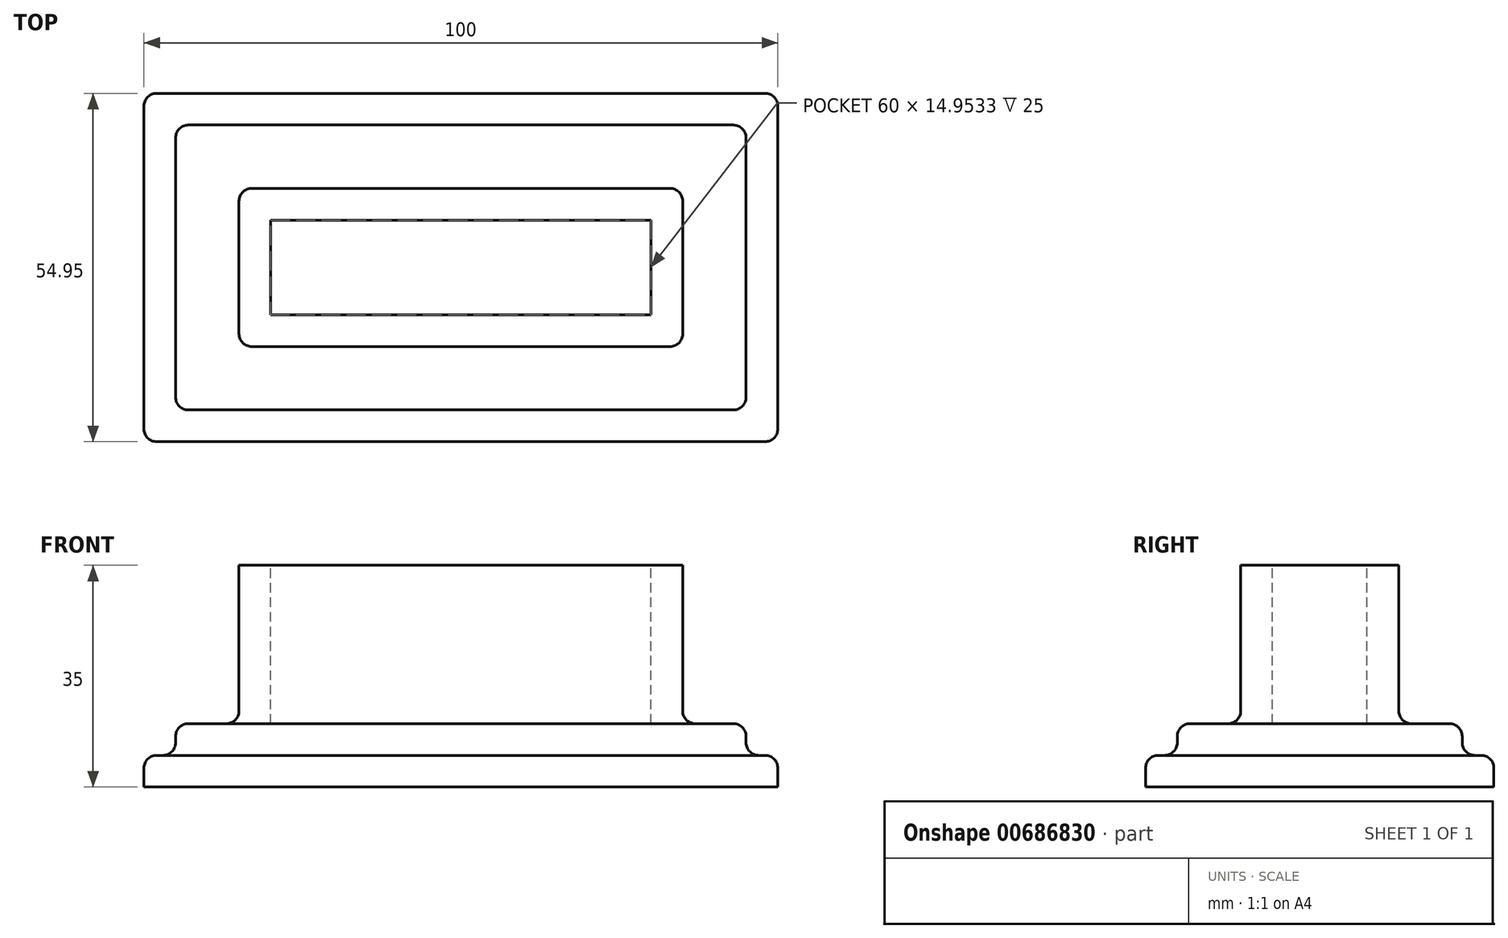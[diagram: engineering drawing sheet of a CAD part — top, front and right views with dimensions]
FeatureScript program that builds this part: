
annotation { "Feature Type Name" : "Feature", "Feature Type Description" : "" }
export const myFeature = defineFeature(function(context is Context, id is Id, definition is map)
    precondition{}
    {
        {
            var Q0;
            Q0=qCreatedBy(makeId("Top.planeOp"),FACE);
            var sketch = newSketch(context, id + "F0", { "sketchPlane" : qUnion([Q0])});
            skLineSegment(sketch, "E0.bottom", {"start": v(-39.07, 25.23) * mm, "end": v(60.93, 25.23) * mm});
            skLineSegment(sketch, "E0.top", {"start": v(-39.07, -29.72) * mm, "end": v(60.93, -29.72) * mm});
            skLineSegment(sketch, "E0.left", {"start": v(-39.07, 25.23) * mm, "end": v(-39.07, -29.72) * mm});
            skLineSegment(sketch, "E0.right", {"start": v(60.93, 25.23) * mm, "end": v(60.93, -29.72) * mm});
            skSolve(sketch);
        }
        {
            var Q0;
            Q0 = qSketchRegion(id + "F0", true);
            extrude(context, id + "F1", {"entities" : qUnion([Q0]), "depth" : 5 * mm, "offsetDistance" : 25 * mm});
        }
        {
            var Q0;
            Q0=makeQuery(id+"F1.opExtrude","CAP_FACE",FACE,{"disambiguationData":[OSD([sQuery(id+"F0.wireOp",EDGE,"E0.bottom"),sQuery(id+"F0.wireOp",EDGE,"E0.top"),sQuery(id+"F0.wireOp",EDGE,"E0.left"),sQuery(id+"F0.wireOp",EDGE,"E0.right")])],"isStart":false});
            var sketch = newSketch(context, id + "F2", { "sketchPlane" : qUnion([Q0])});
            skLineSegment(sketch, "E1.bottom", {"start": v(-34.07, 20.23) * mm, "end": v(55.93, 20.23) * mm});
            skLineSegment(sketch, "E1.top", {"start": v(-34.07, -24.72) * mm, "end": v(55.93, -24.72) * mm});
            skLineSegment(sketch, "E1.left", {"start": v(-34.07, 20.23) * mm, "end": v(-34.07, -24.72) * mm});
            skLineSegment(sketch, "E1.right", {"start": v(55.93, 20.23) * mm, "end": v(55.93, -24.72) * mm});
            skSolve(sketch);
        }
        {
            var Q0;
            Q0 = qSketchRegion(id + "F2", true);
            extrude(context, id + "F3", {"entities" : qUnion([Q0]), "operationType" : NewBodyOperationType.ADD, "depth" : 5 * mm, "offsetDistance" : 25 * mm});
        }
        {
            var Q0;
            Q0=makeQuery(id+"F3.opExtrude","CAP_FACE",FACE,{"disambiguationData":[OSD([sQuery(id+"F2.wireOp",EDGE,"E1.bottom"),sQuery(id+"F2.wireOp",EDGE,"E1.top"),sQuery(id+"F2.wireOp",EDGE,"E1.left"),sQuery(id+"F2.wireOp",EDGE,"E1.right")])],"isStart":false});
            var sketch = newSketch(context, id + "F4", { "sketchPlane" : qUnion([Q0])});
            skLineSegment(sketch, "E2.bottom", {"start": v(-24.07, 10.23) * mm, "end": v(45.93, 10.23) * mm});
            skLineSegment(sketch, "E2.top", {"start": v(-24.07, -14.72) * mm, "end": v(45.93, -14.72) * mm});
            skLineSegment(sketch, "E2.left", {"start": v(-24.07, 10.23) * mm, "end": v(-24.07, -14.72) * mm});
            skLineSegment(sketch, "E2.right", {"start": v(45.93, 10.23) * mm, "end": v(45.93, -14.72) * mm});
            skSolve(sketch);
        }
        {
            var Q0;
            Q0 = qSketchRegion(id + "F4", true);
            extrude(context, id + "F5", {"entities" : qUnion([Q0]), "operationType" : NewBodyOperationType.ADD, "depth" : 25 * mm, "offsetDistance" : 25 * mm});
        }
        {
            var Q0;
            Q0=makeQuery(id+"F1.opExtrude","SWEPT_EDGE",EDGE,{"disambiguationData":[OSD([sQuery(id+"F0.wireOp",EDGE,"E0.bottom"),sQuery(id+"F0.wireOp",EDGE,"E0.right")])]});
            var Q1;
            Q1=makeQuery(id+"F1.opExtrude","SWEPT_EDGE",EDGE,{"disambiguationData":[OSD([sQuery(id+"F0.wireOp",EDGE,"E0.bottom"),sQuery(id+"F0.wireOp",EDGE,"E0.left")])]});
            var Q2;
            Q2=makeQuery(id+"F1.opExtrude","SWEPT_EDGE",EDGE,{"disambiguationData":[OSD([sQuery(id+"F0.wireOp",EDGE,"E0.top"),sQuery(id+"F0.wireOp",EDGE,"E0.left")])]});
            var Q3;
            Q3=makeQuery(id+"F1.opExtrude","SWEPT_EDGE",EDGE,{"disambiguationData":[OSD([sQuery(id+"F0.wireOp",EDGE,"E0.top"),sQuery(id+"F0.wireOp",EDGE,"E0.right")])]});
            var Q4;
            Q4=makeQuery(id+"F5.opExtrude","SWEPT_EDGE",EDGE,{"disambiguationData":[OSD([sQuery(id+"F4.wireOp",EDGE,"E2.top"),sQuery(id+"F4.wireOp",EDGE,"E2.right")])]});
            var Q5;
            Q5=makeQuery(id+"F5.opExtrude","SWEPT_EDGE",EDGE,{"disambiguationData":[OSD([sQuery(id+"F4.wireOp",EDGE,"E2.bottom"),sQuery(id+"F4.wireOp",EDGE,"E2.right")])]});
            var Q6;
            Q6=makeQuery(id+"F3.opExtrude","SWEPT_EDGE",EDGE,{"disambiguationData":[OSD([sQuery(id+"F2.wireOp",EDGE,"E1.bottom"),sQuery(id+"F2.wireOp",EDGE,"E1.right")])]});
            var Q7;
            Q7=makeQuery(id+"F3.opExtrude","SWEPT_EDGE",EDGE,{"disambiguationData":[OSD([sQuery(id+"F2.wireOp",EDGE,"E1.top"),sQuery(id+"F2.wireOp",EDGE,"E1.right")])]});
            var Q8;
            Q8=makeQuery(id+"F5.opExtrude","SWEPT_EDGE",EDGE,{"disambiguationData":[OSD([sQuery(id+"F4.wireOp",EDGE,"E2.top"),sQuery(id+"F4.wireOp",EDGE,"E2.left")])]});
            var Q9;
            Q9=makeQuery(id+"F5.opExtrude","SWEPT_EDGE",EDGE,{"disambiguationData":[OSD([sQuery(id+"F4.wireOp",EDGE,"E2.bottom"),sQuery(id+"F4.wireOp",EDGE,"E2.left")])]});
            var Q10;
            Q10=makeQuery(id+"F3.opExtrude","SWEPT_EDGE",EDGE,{"disambiguationData":[OSD([sQuery(id+"F2.wireOp",EDGE,"E1.top"),sQuery(id+"F2.wireOp",EDGE,"E1.left")])]});
            var Q11;
            Q11=makeQuery(id+"F3.opExtrude","SWEPT_EDGE",EDGE,{"disambiguationData":[OSD([sQuery(id+"F2.wireOp",EDGE,"E1.bottom"),sQuery(id+"F2.wireOp",EDGE,"E1.left")])]});
            var Q12;
            Q12=makeQuery(id+"F3.opExtrude","CAP_EDGE",EDGE,{"disambiguationData":[OSD([sQuery(id+"F2.wireOp",EDGE,"E1.top")])],"isStart":true});
            var Q13;
            Q13=makeQuery(id+"F5.opExtrude","CAP_EDGE",EDGE,{"disambiguationData":[OSD([sQuery(id+"F4.wireOp",EDGE,"E2.top")])],"isStart":true});
            var Q14;
            Q14=makeQuery(id+"F3.opExtrude","CAP_EDGE",EDGE,{"disambiguationData":[OSD([sQuery(id+"F2.wireOp",EDGE,"E1.top")])],"isStart":false});
            var Q15;
            Q15=makeQuery(id+"F1.opExtrude","CAP_EDGE",EDGE,{"disambiguationData":[OSD([sQuery(id+"F0.wireOp",EDGE,"E0.top")])],"isStart":false});
            var Q16;
            Q16=makeQuery(id+"F1.opExtrude","CAP_EDGE",EDGE,{"disambiguationData":[OSD([sQuery(id+"F0.wireOp",EDGE,"E0.right")])],"isStart":false});
            var Q17;
            Q17=makeQuery(id+"F1.opExtrude","CAP_FACE",FACE,{"disambiguationData":[OSD([sQuery(id+"F0.wireOp",EDGE,"E0.bottom"),sQuery(id+"F0.wireOp",EDGE,"E0.top"),sQuery(id+"F0.wireOp",EDGE,"E0.left"),sQuery(id+"F0.wireOp",EDGE,"E0.right")])],"isStart":false});
            var Q18;
            Q18=makeQuery(id+"F5.opExtrude","CAP_EDGE",EDGE,{"disambiguationData":[OSD([sQuery(id+"F4.wireOp",EDGE,"E2.right")])],"isStart":true});
            var Q19;
            Q19=makeQuery(id+"F3.opExtrude","CAP_FACE",FACE,{"disambiguationData":[OSD([sQuery(id+"F2.wireOp",EDGE,"E1.bottom"),sQuery(id+"F2.wireOp",EDGE,"E1.top"),sQuery(id+"F2.wireOp",EDGE,"E1.left"),sQuery(id+"F2.wireOp",EDGE,"E1.right")])],"isStart":false});
            fillet(context, id + "F6", {"entities" : qUnion([Q0, Q1, Q2, Q3, Q4, Q5, Q6, Q7, Q8, Q9, Q10, Q11, Q12, Q13, Q14, Q15, Q16, Q17, Q18, Q19]), "radius" : 2 * mm, "tangentPropagation" : true, "allowEdgeOverflow" : false});
        }
        {
            var Q0;
            Q0=makeQuery(id+"F5.opExtrude","CAP_FACE",FACE,{"disambiguationData":[OSD([sQuery(id+"F4.wireOp",EDGE,"E2.bottom"),sQuery(id+"F4.wireOp",EDGE,"E2.top"),sQuery(id+"F4.wireOp",EDGE,"E2.left"),sQuery(id+"F4.wireOp",EDGE,"E2.right")])],"isStart":false});
            var sketch = newSketch(context, id + "F7", { "sketchPlane" : qUnion([Q0])});
            skLineSegment(sketch, "E3.bottom", {"start": v(-19.07, 5.23) * mm, "end": v(40.93, 5.23) * mm});
            skLineSegment(sketch, "E3.top", {"start": v(-19.07, -9.72) * mm, "end": v(40.93, -9.72) * mm});
            skLineSegment(sketch, "E3.left", {"start": v(-19.07, 5.23) * mm, "end": v(-19.07, -9.72) * mm});
            skLineSegment(sketch, "E3.right", {"start": v(40.93, 5.23) * mm, "end": v(40.93, -9.72) * mm});
            skSolve(sketch);
        }
        {
            var Q0;
            Q0 = qSketchRegion(id + "F7", true);
            extrude(context, id + "F8", {"entities" : qUnion([Q0]), "operationType" : NewBodyOperationType.REMOVE, "oppositeDirection" : true, "depth" : 25 * mm, "offsetDistance" : 25 * mm});
        }
    });
